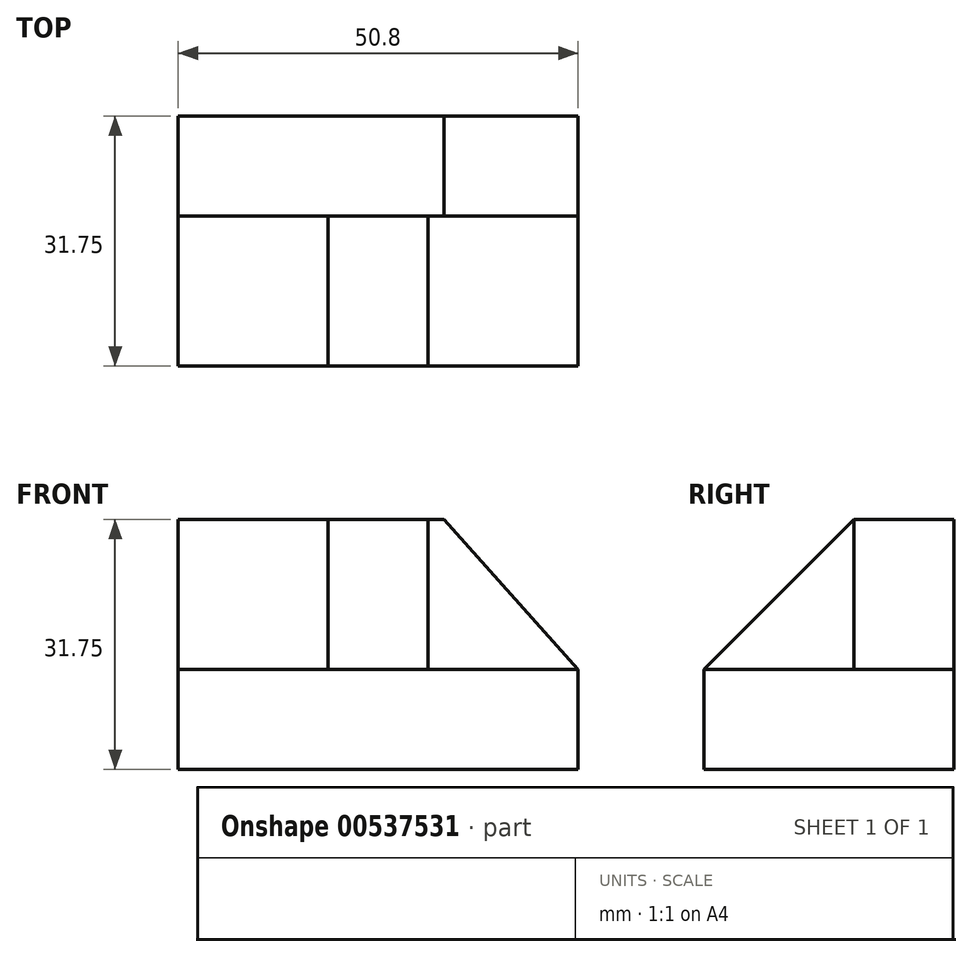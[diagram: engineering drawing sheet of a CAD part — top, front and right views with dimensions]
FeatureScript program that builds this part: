
annotation { "Feature Type Name" : "Feature", "Feature Type Description" : "" }
export const myFeature = defineFeature(function(context is Context, id is Id, definition is map)
    precondition{}
    {
        {
            var Q0;
            Q0=qCreatedBy(makeId("Right.planeOp"),FACE);
            var sketch = newSketch(context, id + "F0", { "sketchPlane" : qUnion([Q0])});
            skLineSegment(sketch, "E0", {"start": v(0, 0) * mm, "end": v(31.75, 0) * mm});
            skLineSegment(sketch, "E1", {"start": v(31.75, 0) * mm, "end": v(31.75, 31.75) * mm});
            skLineSegment(sketch, "E2", {"start": v(31.75, 31.75) * mm, "end": v(19.05, 31.75) * mm});
            skLineSegment(sketch, "E3", {"start": v(19.05, 31.75) * mm, "end": v(19.05, 12.7) * mm});
            skLineSegment(sketch, "E4", {"start": v(19.05, 12.7) * mm, "end": v(0, 12.7) * mm});
            skLineSegment(sketch, "E5", {"start": v(0, 12.7) * mm, "end": v(0, 0) * mm});
            skSolve(sketch);
        }
        {
            var Q0;
            Q0=makeQuery(id+"F0.imprint","IMPRINT",FACE,{"disambiguationData":[TD([[makeQuery(id+"F0.imprint","IMPRINT",EDGE,{"derivedFrom":sQuery(id+"F0.wireOp",EDGE,"E0")}),1.0]])]});
            extrude(context, id + "F1", {"entities" : qUnion([Q0]), "depth" : 50.8 * mm, "offsetDistance" : 25.4 * mm});
        }
        {
            var Q0;
            Q0=makeQuery(id+"F1.opExtrude","SWEPT_FACE",FACE,{"disambiguationData":[OSD([sQuery(id+"F0.wireOp",EDGE,"E3")])]});
            var sketch = newSketch(context, id + "F2", { "sketchPlane" : qUnion([Q0])});
            skLineSegment(sketch, "E6", {"start": v(33.76, 31.75) * mm, "end": v(50.8, 12.7) * mm});
            skSolve(sketch);
        }
        {
            var Q0;
            {var subQ0=sQuery(id+"F2.wireOp",EDGE,"E6");Q0=makeQuery(id+"F2.imprint","IMPRINT",FACE,{"disambiguationData":[TD([[makeQuery(id+"F2.imprint","IMPRINT",EDGE,{"derivedFrom":subQ0}),1.0]])]});}
            extrude(context, id + "F3", {"entities" : qUnion([Q0]), "operationType" : NewBodyOperationType.REMOVE, "oppositeDirection" : true, "depth" : 12.7 * mm, "offsetDistance" : 25.4 * mm});
        }
        {
            var Q0;
            Q0=makeQuery(id+"F1.opExtrude","SWEPT_FACE",FACE,{"disambiguationData":[OSD([sQuery(id+"F0.wireOp",EDGE,"E3")])]});
            var sketch = newSketch(context, id + "F4", { "sketchPlane" : qUnion([Q0])});
            skLineSegment(sketch, "E7", {"start": v(31.75, 31.75) * mm, "end": v(31.75, 12.7) * mm});
            skLineSegment(sketch, "E8", {"start": v(19.05, 31.75) * mm, "end": v(19.05, 12.7) * mm});
            skSolve(sketch);
        }
        {
            var Q0;
            {var subQ0=sQuery(id+"F4.wireOp",EDGE,"E7");Q0=makeQuery(id+"F4.imprint","IMPRINT",FACE,{"disambiguationData":[TD([[makeQuery(id+"F4.imprint","IMPRINT",EDGE,{"derivedFrom":subQ0}),-1.0]])]});}
            extrude(context, id + "F5", {"entities" : qUnion([Q0]), "operationType" : NewBodyOperationType.ADD, "depth" : 19.05 * mm, "offsetDistance" : 25.4 * mm});
        }
        {
            var Q0;
            Q0=makeQuery(id+"F5.opExtrude","SWEPT_FACE",FACE,{"disambiguationData":[OSD([sQuery(id+"F4.wireOp",EDGE,"E7")])]});
            var sketch = newSketch(context, id + "F6", { "sketchPlane" : qUnion([Q0])});
            skLineSegment(sketch, "E9", {"start": v(19.05, 31.75) * mm, "end": v(0, 12.7) * mm});
            skSolve(sketch);
        }
        {
            var Q0;
            Q0=makeQuery(id+"F6.imprint","IMPRINT",FACE,{"disambiguationData":[TD([[makeQuery(id+"F6.imprint","IMPRINT",EDGE,{"derivedFrom":sQuery(id+"F6.wireOp",EDGE,"E9")}),-1.0]])]});
            extrude(context, id + "F7", {"entities" : qUnion([Q0]), "operationType" : NewBodyOperationType.REMOVE, "oppositeDirection" : true, "depth" : 12.7 * mm, "offsetDistance" : 25.4 * mm});
        }
    });
